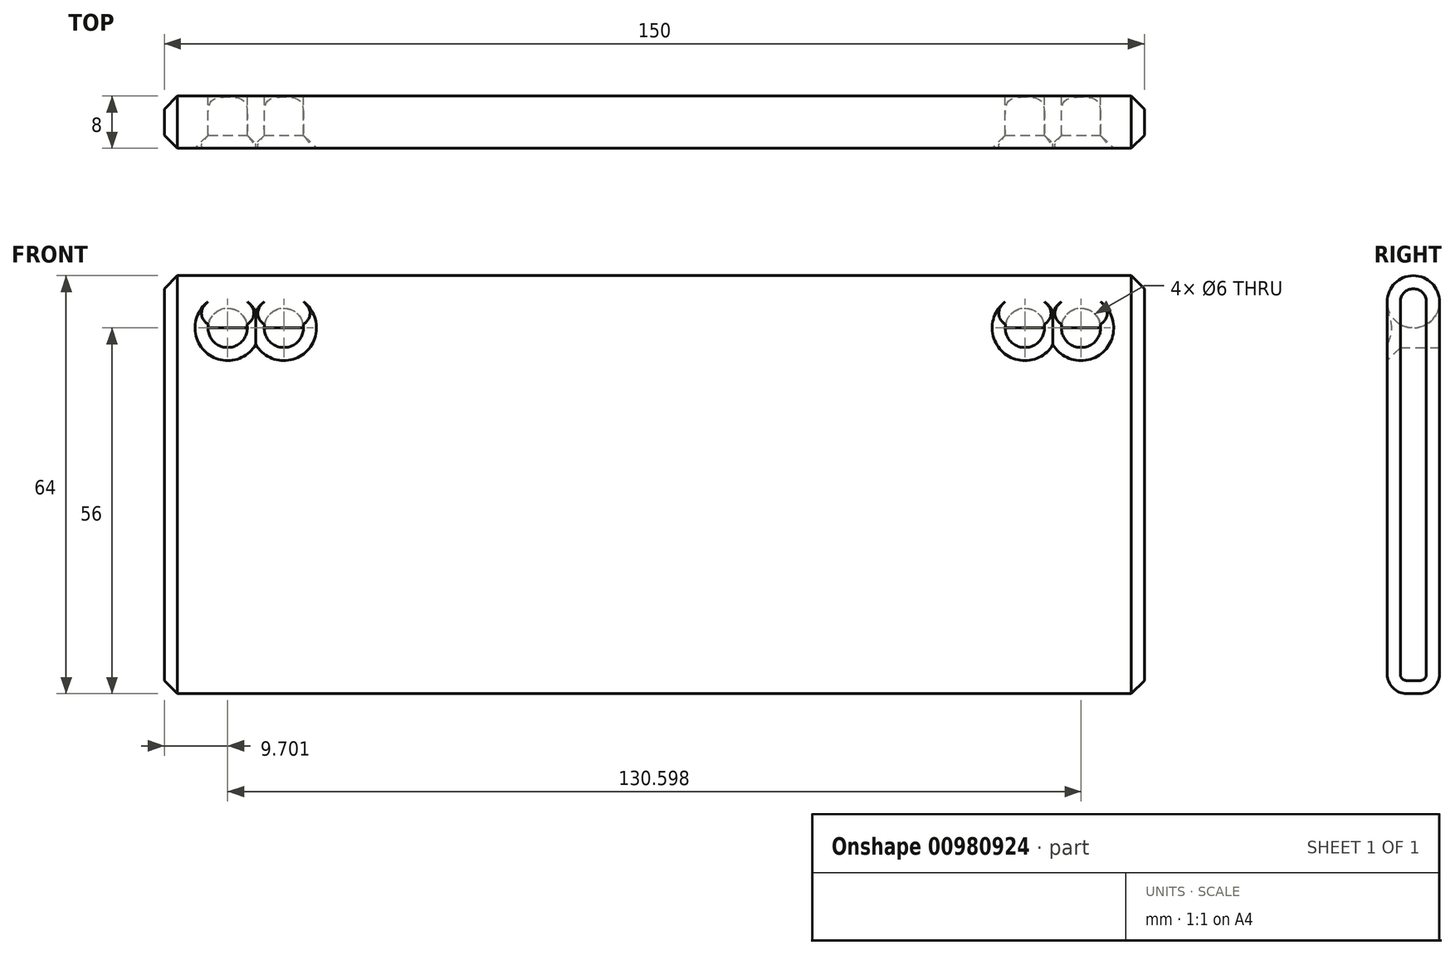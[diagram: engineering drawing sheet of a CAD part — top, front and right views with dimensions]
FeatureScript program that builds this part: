
annotation { "Feature Type Name" : "Feature", "Feature Type Description" : "" }
export const myFeature = defineFeature(function(context is Context, id is Id, definition is map)
    precondition{}
    {
        {
            var Q0;
            Q0=qCreatedBy(makeId("Front.planeOp"),FACE);
            var sketch = newSketch(context, id + "F0", { "sketchPlane" : qUnion([Q0])});
            skLineSegment(sketch, "E0.bottom", {"start": v(75, 30) * mm, "end": v(-75, 30) * mm});
            skLineSegment(sketch, "E0.top", {"start": v(75, -30) * mm, "end": v(-75, -30) * mm});
            skLineSegment(sketch, "E0.left", {"start": v(75, 30) * mm, "end": v(75, -30) * mm});
            skLineSegment(sketch, "E0.right", {"start": v(-75, 30) * mm, "end": v(-75, -30) * mm});
            skPoint(sketch, "E0.middle", {"position": v(0, 0) * mm});
            skLineSegment(sketch, "E1", {"start": v(0, 30) * mm, "end": v(0, -43.05) * mm, "construction": true});
            skLineSegment(sketch, "E2", {"start": v(-75, 26) * mm, "end": v(75, 26) * mm, "construction": true});
            skCircle(sketch, "E3", {"center": v(-65.3, 26) * mm, "radius": 3 * mm});
            skCircle(sketch, "E4", {"center": v(-56.7, 26) * mm, "radius": 3 * mm});
            skCircle(sketch, "E5.MirrorC", {"center": v(56.7, 26) * mm, "radius": 3 * mm});
            skCircle(sketch, "E6.MirrorC", {"center": v(65.3, 26) * mm, "radius": 3 * mm});
            skSolve(sketch);
        }
        {
            var Q0;
            Q0=makeQuery(id+"F0.imprint","IMPRINT",FACE,{"disambiguationData":[TD([[makeQuery(id+"F0.imprint","IMPRINT",EDGE,{"derivedFrom":sQuery(id+"F0.wireOp",EDGE,"E0.bottom")}),1.0]])]});
            extrude(context, id + "F1", {"entities" : qUnion([Q0]), "endBound" : BoundingType.SYMMETRIC, "depth" : 8 * mm, "offsetDistance" : 25 * mm});
        }
        {
            var Q0;
            Q0=makeQuery(id+"F1.opExtrude","SWEPT_FACE",FACE,{"disambiguationData":[OSD([sQuery(id+"F0.wireOp",EDGE,"E0.right")])]});
            var sketch = newSketch(context, id + "F2", { "sketchPlane" : qUnion([Q0])});
            skCircle(sketch, "E7", {"center": v(0, 30) * mm, "radius": 4 * mm});
            skSolve(sketch);
        }
        {
            var Q0;
            Q0 = qSketchRegion(id + "F2", true);
            extrude(context, id + "F3", {"entities" : qUnion([Q0]), "operationType" : NewBodyOperationType.ADD, "oppositeDirection" : true, "depth" : 150 * mm, "offsetDistance" : 25 * mm});
        }
        {
            var Q0;
            Q0=makeQuery(id+"F1.opExtrude","CAP_EDGE",EDGE,{"disambiguationData":[OSD([sQuery(id+"F0.wireOp",EDGE,"E0.top")])],"isStart":true});
            var Q1;
            Q1=makeQuery(id+"F1.opExtrude","CAP_EDGE",EDGE,{"disambiguationData":[OSD([sQuery(id+"F0.wireOp",EDGE,"E0.top")])],"isStart":false});
            fillet(context, id + "F4", {"entities" : qUnion([Q0, Q1]), "radius" : 3 * mm, "tangentPropagation" : true, "allowEdgeOverflow" : false});
        }
        {
            var Q0;
            Q0=makeQuery(id+"F1.opExtrude","CAP_EDGE",EDGE,{"disambiguationData":[OSD([sQuery(id+"F0.wireOp",EDGE,"E3")])],"isStart":false});
            var Q1;
            Q1=makeQuery(id+"F1.opExtrude","CAP_EDGE",EDGE,{"disambiguationData":[OSD([sQuery(id+"F0.wireOp",EDGE,"E4")])],"isStart":false});
            var Q2;
            Q2=makeQuery(id+"F1.opExtrude","CAP_EDGE",EDGE,{"disambiguationData":[OSD([sQuery(id+"F0.wireOp",EDGE,"E5.MirrorC")])],"isStart":false});
            var Q3;
            Q3=makeQuery(id+"F1.opExtrude","CAP_EDGE",EDGE,{"disambiguationData":[OSD([sQuery(id+"F0.wireOp",EDGE,"E6.MirrorC")])],"isStart":false});
            chamfer(context, id + "F5", {"entities" : qUnion([Q0, Q1, Q2, Q3]), "width" : 2 * mm, "tangentPropagation" : true});
        }
        {
            var Q0;
            Q0=makeQuery(id+"F1.opExtrude","CAP_EDGE",EDGE,{"disambiguationData":[OSD([sQuery(id+"F0.wireOp",EDGE,"E0.right")])],"isStart":true});
            var Q1;
            Q1=makeQuery(id+"F1.opExtrude","CAP_EDGE",EDGE,{"disambiguationData":[OSD([sQuery(id+"F0.wireOp",EDGE,"E0.left")])],"isStart":true});
            chamfer(context, id + "F6", {"entities" : qUnion([Q0, Q1]), "width" : 2 * mm, "tangentPropagation" : true});
        }
    });
